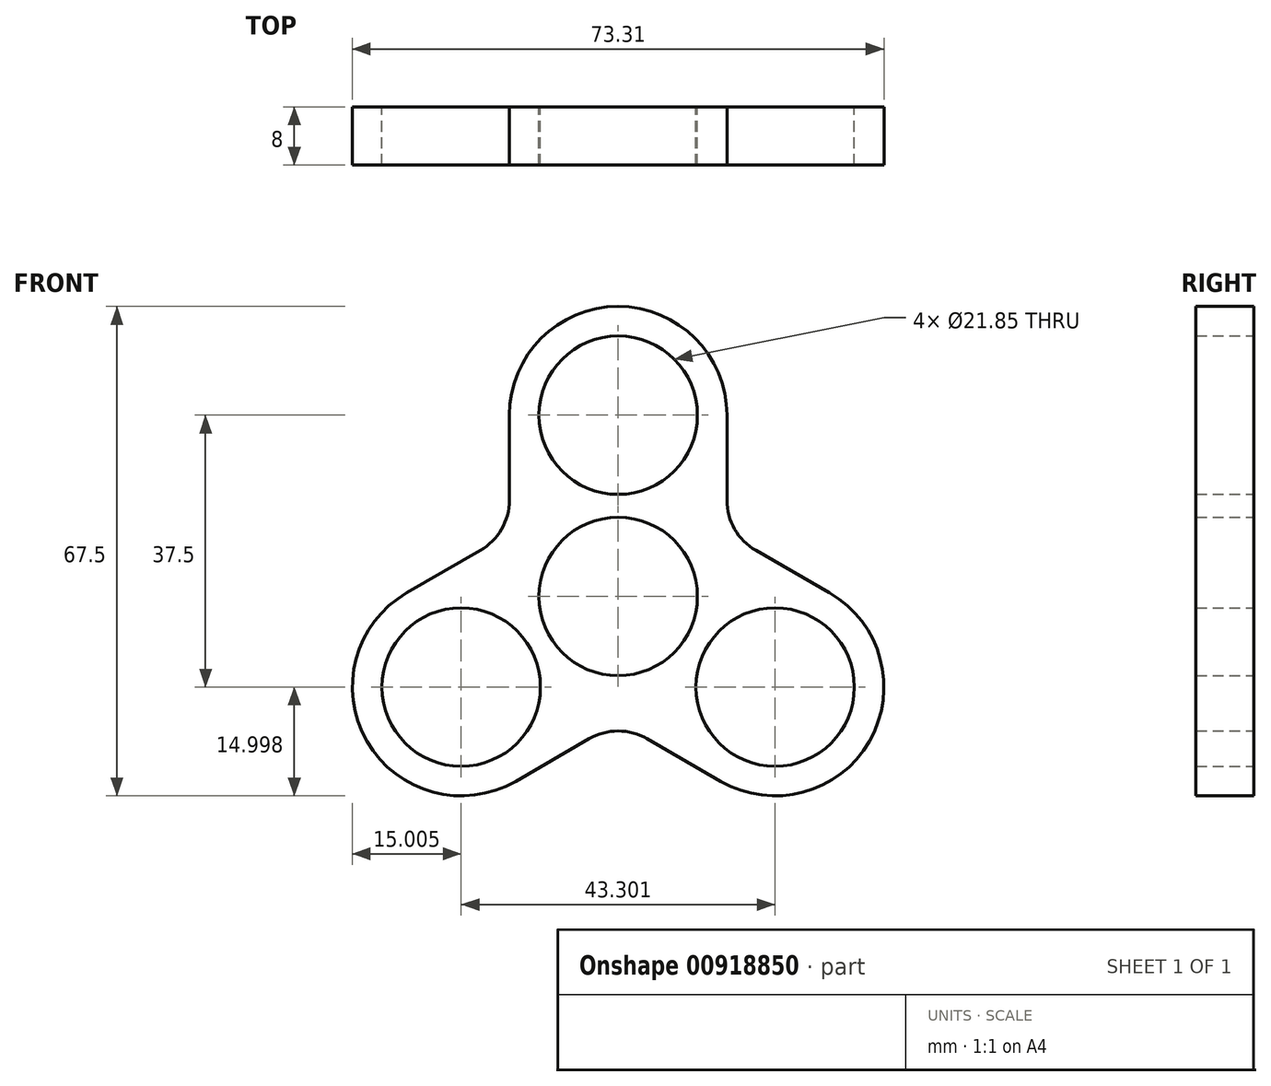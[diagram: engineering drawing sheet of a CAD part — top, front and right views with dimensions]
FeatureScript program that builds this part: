
annotation { "Feature Type Name" : "Feature", "Feature Type Description" : "" }
export const myFeature = defineFeature(function(context is Context, id is Id, definition is map)
    precondition{}
    {
        {
            var Q0;
            Q0=qCreatedBy(makeId("Front.planeOp"),FACE);
            var sketch = newSketch(context, id + "F0", { "sketchPlane" : qUnion([Q0])});
            skCircle(sketch, "E0", {"center": v(-304.85, -30.8) * mm, "radius": 10.93 * mm});
            skCircle(sketch, "E1", {"center": v(-304.85, -55.8) * mm, "radius": 10.93 * mm});
            skArc(sketch, "E2", {"start": v(-319.85, -30.8) * mm, "mid": v(-304.85, -15.8) * mm, "end": v(-289.85, -30.8) * mm});
            skArc(sketch, "E3", {"start": v(-319.85, -55.8) * mm, "mid": v(-304.85, -70.8) * mm, "end": v(-289.85, -55.8) * mm});
            skLineSegment(sketch, "E4", {"start": v(-319.85, -42.52) * mm, "end": v(-319.85, -30.8) * mm});
            skLineSegment(sketch, "E5", {"start": v(-289.85, -30.8) * mm, "end": v(-289.85, -42.52) * mm});
            skArc(sketch, "E6.1.0", {"start": v(-319, -81.3) * mm, "mid": v(-339.5, -75.8) * mm, "end": v(-334, -55.31) * mm});
            skCircle(sketch, "E6.1.1", {"center": v(-326.5, -68.3) * mm, "radius": 10.92 * mm});
            skCircle(sketch, "E6.1.2", {"center": v(-304.85, -55.8) * mm, "radius": 10.92 * mm});
            skArc(sketch, "E6.1.3", {"start": v(-297.35, -68.8) * mm, "mid": v(-291.86, -48.3) * mm, "end": v(-312.35, -42.81) * mm});
            skLineSegment(sketch, "E6.1.4", {"start": v(-308.85, -75.43) * mm, "end": v(-319, -81.3) * mm});
            skLineSegment(sketch, "E6.1.5", {"start": v(-334, -55.31) * mm, "end": v(-323.85, -49.45) * mm});
            skArc(sketch, "E6.2.0", {"start": v(-275.7, -55.31) * mm, "mid": v(-270.21, -75.8) * mm, "end": v(-290.7, -81.3) * mm});
            skCircle(sketch, "E6.2.1", {"center": v(-283.2, -68.3) * mm, "radius": 10.93 * mm});
            skArc(sketch, "E6.2.3", {"start": v(-297.35, -42.81) * mm, "mid": v(-317.84, -48.3) * mm, "end": v(-312.35, -68.8) * mm});
            skLineSegment(sketch, "E6.2.4", {"start": v(-285.85, -49.45) * mm, "end": v(-275.7, -55.31) * mm});
            skLineSegment(sketch, "E6.2.5", {"start": v(-290.7, -81.3) * mm, "end": v(-300.85, -75.43) * mm});
            skPoint(sketch, "E7", {"position": v(-289.85, -47.14) * mm});
            skPoint(sketch, "E8.newPointA", {"position": v(-289.85, -55.8) * mm});
            skPoint(sketch, "E8.newPointB", {"position": v(-297.35, -42.81) * mm});
            skArc(sketch, "E8.filletArc", {"start": v(-289.85, -42.52) * mm, "mid": v(-288.78, -46.52) * mm, "end": v(-285.85, -49.45) * mm});
            skPoint(sketch, "E9", {"position": v(-319.85, -47.14) * mm});
            skPoint(sketch, "E10", {"position": v(-304.85, -73.12) * mm});
            skPoint(sketch, "E11.newPointA", {"position": v(-319.85, -55.8) * mm});
            skPoint(sketch, "E11.newPointB", {"position": v(-312.35, -42.81) * mm});
            skArc(sketch, "E11.filletArc", {"start": v(-323.85, -49.45) * mm, "mid": v(-320.93, -46.52) * mm, "end": v(-319.85, -42.52) * mm});
            skPoint(sketch, "E12.newPointA", {"position": v(-312.35, -68.8) * mm});
            skPoint(sketch, "E12.newPointB", {"position": v(-297.35, -68.8) * mm});
            skArc(sketch, "E12.filletArc", {"start": v(-300.85, -75.43) * mm, "mid": v(-304.85, -74.36) * mm, "end": v(-308.85, -75.43) * mm});
            skSolve(sketch);
        }
        {
            var Q0;
            Q0 = qSketchRegion(id + "F0", true);
            var Q1;
            {var subQ10=sQuery(id+"F0.wireOp",EDGE,"E3");Q1=makeQuery(id+"F0.imprint","IMPRINT",FACE,{"disambiguationData":[TD([[makeQuery(id+"F0.imprint","IMPRINT",EDGE,{"derivedFrom":subQ10}),1.0]])]});}
            extrude(context, id + "F1", {"entities" : qUnion([Q0, Q1]), "depth" : 8 * mm, "offsetDistance" : 25 * mm});
        }
    });
